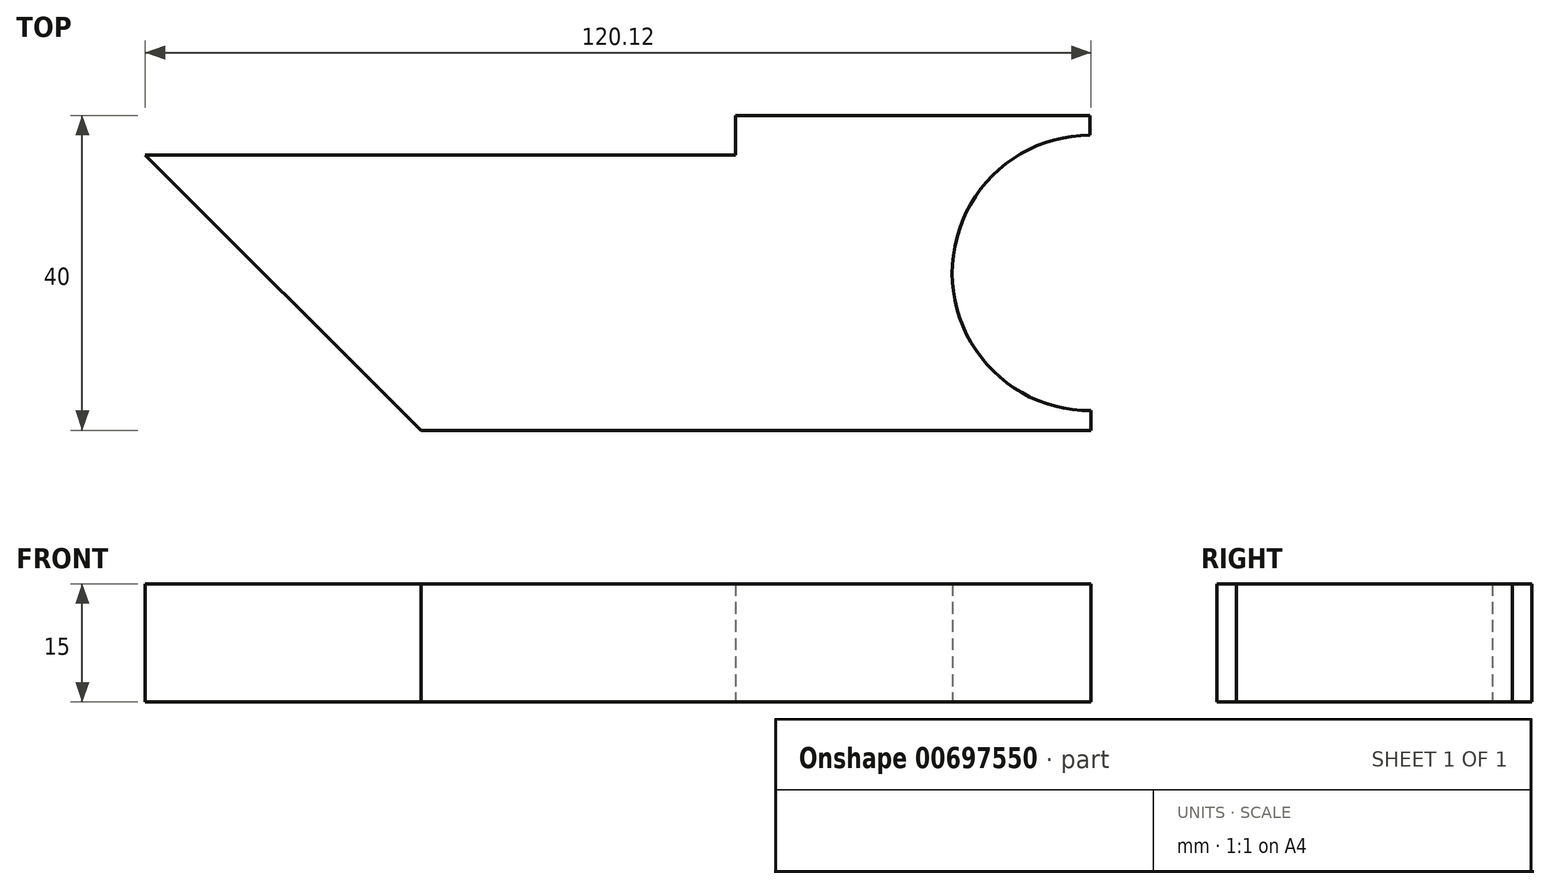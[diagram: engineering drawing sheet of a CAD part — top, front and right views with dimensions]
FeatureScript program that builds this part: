
annotation { "Feature Type Name" : "Feature", "Feature Type Description" : "" }
export const myFeature = defineFeature(function(context is Context, id is Id, definition is map)
    precondition{}
    {
        {
            var Q0;
            Q0=qCreatedBy(makeId("Top.planeOp"),FACE);
            var sketch = newSketch(context, id + "F0", { "sketchPlane" : qUnion([Q0])});
            skArc(sketch, "E0", {"start": v(55.73, 17.5) * mm, "mid": v(38.23, -0.06) * mm, "end": v(55.85, -17.5) * mm});
            skLineSegment(sketch, "E1", {"start": v(-64.27, 15) * mm, "end": v(-29.27, -20) * mm});
            skLineSegment(sketch, "E2", {"start": v(-64.27, 15) * mm, "end": v(10.73, 15) * mm});
            skLineSegment(sketch, "E3", {"start": v(10.73, 15) * mm, "end": v(10.73, 20) * mm});
            skLineSegment(sketch, "E4", {"start": v(10.73, 20) * mm, "end": v(55.73, 20) * mm});
            skLineSegment(sketch, "E5", {"start": v(55.73, 20) * mm, "end": v(55.73, 17.5) * mm});
            skLineSegment(sketch, "E6", {"start": v(55.85, -17.5) * mm, "end": v(55.85, -20) * mm});
            skLineSegment(sketch, "E7", {"start": v(55.85, -20) * mm, "end": v(-29.27, -20) * mm});
            skSolve(sketch);
        }
        {
            var Q0;
            Q0 = qSketchRegion(id + "F0", true);
            extrude(context, id + "F1", {"entities" : qUnion([Q0]), "endBound" : BoundingType.SYMMETRIC, "depth" : 15 * mm, "offsetDistance" : 25 * mm});
        }
    });
